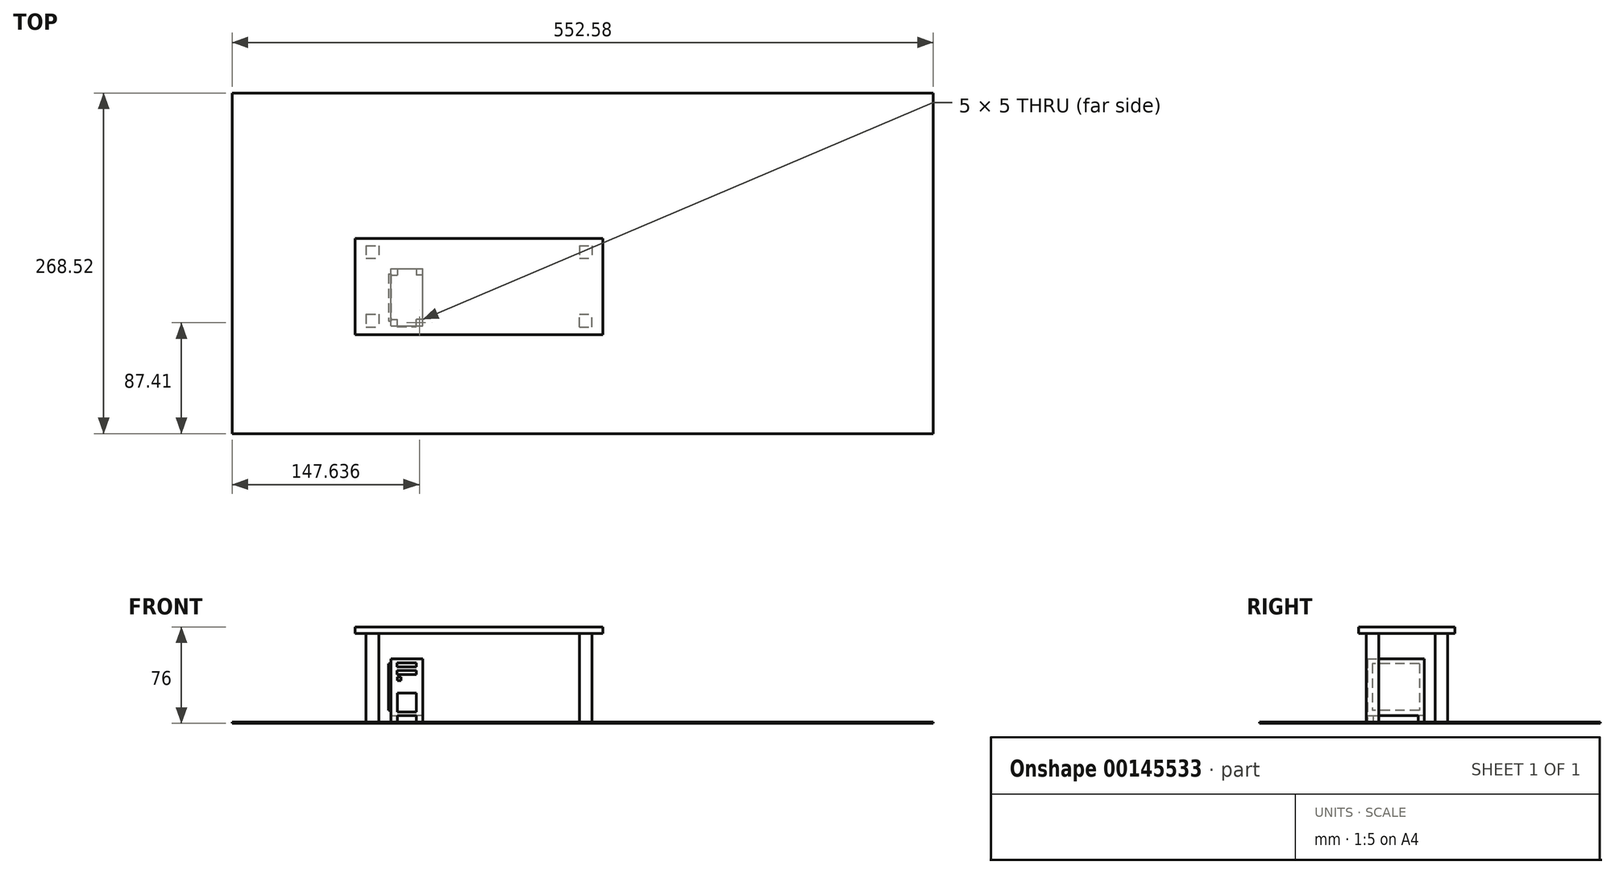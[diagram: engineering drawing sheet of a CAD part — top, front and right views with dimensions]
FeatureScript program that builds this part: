
annotation { "Feature Type Name" : "Feature", "Feature Type Description" : "" }
export const myFeature = defineFeature(function(context is Context, id is Id, definition is map)
    precondition{}
    {
        {
            var Q0;
            Q0=qCreatedBy(makeId("Front.planeOp"),FACE);
            var sketch = newSketch(context, id + "F0", { "sketchPlane" : qUnion([Q0])});
            skLineSegment(sketch, "E0.bottom", {"start": v(-65.78, 17.75) * mm, "end": v(-40.78, 17.75) * mm});
            skLineSegment(sketch, "E0.top", {"start": v(-65.78, -27.25) * mm, "end": v(-40.78, -27.25) * mm});
            skLineSegment(sketch, "E0.left", {"start": v(-65.78, 17.75) * mm, "end": v(-65.78, -27.25) * mm});
            skLineSegment(sketch, "E0.right", {"start": v(-40.78, 17.75) * mm, "end": v(-40.78, -27.25) * mm});
            skSolve(sketch);
        }
        {
            var Q0;
            Q0=makeQuery(id+"F0.imprint","IMPRINT",FACE,{"disambiguationData":[TD([[makeQuery(id+"F0.imprint","IMPRINT",EDGE,{"derivedFrom":sQuery(id+"F0.wireOp",EDGE,"E0.bottom")}),-1.0]])]});
            extrude(context, id + "F1", {"entities" : qUnion([Q0]), "depth" : 45 * mm});
        }
        {
            var Q0;
            Q0=makeQuery(id+"F1.opExtrude","SWEPT_FACE",FACE,{"disambiguationData":[OSD([sQuery(id+"F0.wireOp",EDGE,"E0.left")])]});
            var sketch = newSketch(context, id + "F2", { "sketchPlane" : qUnion([Q0])});
            skLineSegment(sketch, "E1.bottom", {"start": v(4.1, 13.7) * mm, "end": v(41.11, 13.7) * mm});
            skLineSegment(sketch, "E1.top", {"start": v(4.1, -23.11) * mm, "end": v(41.11, -23.11) * mm});
            skLineSegment(sketch, "E1.left", {"start": v(4.1, 13.7) * mm, "end": v(4.1, -23.11) * mm});
            skLineSegment(sketch, "E1.right", {"start": v(41.11, 13.7) * mm, "end": v(41.11, -23.11) * mm});
            skSolve(sketch);
        }
        {
            var Q0;
            Q0=makeQuery(id+"F2.imprint","IMPRINT",FACE,{"disambiguationData":[TD([[makeQuery(id+"F2.imprint","IMPRINT",EDGE,{"derivedFrom":sQuery(id+"F2.wireOp",EDGE,"E1.bottom")}),-1.0]])]});
            extrude(context, id + "F3", {"entities" : qUnion([Q0]), "depth" : 2 * mm});
        }
        {
            var Q0;
            Q0=makeQuery(id+"F1.opExtrude","CAP_FACE",FACE,{"disambiguationData":[OSD([sQuery(id+"F0.wireOp",EDGE,"E0.bottom"),sQuery(id+"F0.wireOp",EDGE,"E0.top"),sQuery(id+"F0.wireOp",EDGE,"E0.left"),sQuery(id+"F0.wireOp",EDGE,"E0.right")])],"isStart":false});
            var sketch = newSketch(context, id + "F4", { "sketchPlane" : qUnion([Q0])});
            skLineSegment(sketch, "E2.bottom", {"start": v(-60.89, 14.33) * mm, "end": v(-45.89, 14.33) * mm});
            skLineSegment(sketch, "E2.top", {"start": v(-60.89, 11.33) * mm, "end": v(-45.89, 11.33) * mm});
            skLineSegment(sketch, "E2.left", {"start": v(-60.89, 14.33) * mm, "end": v(-60.89, 11.33) * mm});
            skLineSegment(sketch, "E2.right", {"start": v(-45.89, 14.33) * mm, "end": v(-45.89, 11.33) * mm});
            skLineSegment(sketch, "E3.bottom", {"start": v(-60.89, 8.33) * mm, "end": v(-45.89, 8.33) * mm});
            skLineSegment(sketch, "E3.top", {"start": v(-60.89, 5.33) * mm, "end": v(-45.89, 5.33) * mm});
            skLineSegment(sketch, "E3.left", {"start": v(-60.89, 8.33) * mm, "end": v(-60.89, 5.33) * mm});
            skLineSegment(sketch, "E3.right", {"start": v(-45.89, 8.33) * mm, "end": v(-45.89, 5.33) * mm});
            skSolve(sketch);
        }
        {
            var Q0;
            Q0 = qSketchRegion(id + "F4", true);
            extrude(context, id + "F5", {"entities" : qUnion([Q0]), "depth" : 0.5 * mm});
        }
        {
            var Q0;
            Q0=makeQuery(id+"F1.opExtrude","CAP_FACE",FACE,{"disambiguationData":[OSD([sQuery(id+"F0.wireOp",EDGE,"E0.bottom"),sQuery(id+"F0.wireOp",EDGE,"E0.top"),sQuery(id+"F0.wireOp",EDGE,"E0.left"),sQuery(id+"F0.wireOp",EDGE,"E0.right")])],"isStart":false});
            var sketch = newSketch(context, id + "F6", { "sketchPlane" : qUnion([Q0])});
            skLineSegment(sketch, "E4.bottom", {"start": v(-60.78, -24.38) * mm, "end": v(-45.78, -24.38) * mm});
            skLineSegment(sketch, "E4.top", {"start": v(-60.78, -9.38) * mm, "end": v(-45.78, -9.38) * mm});
            skLineSegment(sketch, "E4.left", {"start": v(-60.78, -24.38) * mm, "end": v(-60.78, -9.38) * mm});
            skLineSegment(sketch, "E4.right", {"start": v(-45.78, -24.38) * mm, "end": v(-45.78, -9.38) * mm});
            skSolve(sketch);
        }
        {
            var Q0;
            Q0=makeQuery(id+"F6.imprint","IMPRINT",FACE,{"disambiguationData":[TD([[makeQuery(id+"F6.imprint","IMPRINT",EDGE,{"derivedFrom":sQuery(id+"F6.wireOp",EDGE,"E4.bottom")}),1.0]])]});
            extrude(context, id + "F7", {"entities" : qUnion([Q0]), "depth" : 0.5 * mm});
        }
        {
            var Q0;
            Q0=makeQuery(id+"F1.opExtrude","CAP_FACE",FACE,{"disambiguationData":[OSD([sQuery(id+"F0.wireOp",EDGE,"E0.bottom"),sQuery(id+"F0.wireOp",EDGE,"E0.top"),sQuery(id+"F0.wireOp",EDGE,"E0.left"),sQuery(id+"F0.wireOp",EDGE,"E0.right")])],"isStart":false});
            var sketch = newSketch(context, id + "F8", { "sketchPlane" : qUnion([Q0])});
            skLineSegment(sketch, "E5.bottom", {"start": v(-60.82, 3.4) * mm, "end": v(-57.82, 3.4) * mm});
            skLineSegment(sketch, "E5.top", {"start": v(-60.82, 0.4) * mm, "end": v(-57.82, 0.4) * mm});
            skLineSegment(sketch, "E5.left", {"start": v(-60.82, 3.4) * mm, "end": v(-60.82, 0.4) * mm});
            skLineSegment(sketch, "E5.right", {"start": v(-57.82, 3.4) * mm, "end": v(-57.82, 0.4) * mm});
            skSolve(sketch);
        }
        {
            var Q0;
            Q0=makeQuery(id+"F8.imprint","IMPRINT",FACE,{"disambiguationData":[TD([[makeQuery(id+"F8.imprint","IMPRINT",EDGE,{"derivedFrom":sQuery(id+"F8.wireOp",EDGE,"E5.bottom")}),-1.0]])]});
            extrude(context, id + "F9", {"entities" : qUnion([Q0]), "depth" : 0.5 * mm});
        }
        {
            var Q0;
            Q0=makeQuery(id+"F9.opExtrude","CAP_FACE",FACE,{"disambiguationData":[OSD([sQuery(id+"F8.wireOp",EDGE,"E5.bottom"),sQuery(id+"F8.wireOp",EDGE,"E5.top"),sQuery(id+"F8.wireOp",EDGE,"E5.left"),sQuery(id+"F8.wireOp",EDGE,"E5.right")])],"isStart":false});
            var sketch = newSketch(context, id + "F10", { "sketchPlane" : qUnion([Q0])});
            skSolve(sketch);
        }
        {
            var Q0;
            Q0=makeQuery(id+"F1.opExtrude","SWEPT_FACE",FACE,{"disambiguationData":[OSD([sQuery(id+"F0.wireOp",EDGE,"E0.top")])]});
            var sketch = newSketch(context, id + "F11", { "sketchPlane" : qUnion([Q0])});
            skLineSegment(sketch, "E6.bottom", {"start": v(-65.78, 45) * mm, "end": v(-60.78, 45) * mm});
            skLineSegment(sketch, "E6.top", {"start": v(-65.78, 40) * mm, "end": v(-60.78, 40) * mm});
            skLineSegment(sketch, "E6.left", {"start": v(-65.78, 45) * mm, "end": v(-65.78, 40) * mm});
            skLineSegment(sketch, "E6.right", {"start": v(-60.78, 45) * mm, "end": v(-60.78, 40) * mm});
            skLineSegment(sketch, "E7.bottom", {"start": v(-40.78, 45) * mm, "end": v(-45.78, 45) * mm});
            skLineSegment(sketch, "E7.top", {"start": v(-40.78, 40) * mm, "end": v(-45.78, 40) * mm});
            skLineSegment(sketch, "E7.left", {"start": v(-40.78, 45) * mm, "end": v(-40.78, 40) * mm});
            skLineSegment(sketch, "E7.right", {"start": v(-45.78, 45) * mm, "end": v(-45.78, 40) * mm});
            skLineSegment(sketch, "E8.bottom", {"start": v(-65.78, 0) * mm, "end": v(-60.78, 0) * mm});
            skLineSegment(sketch, "E8.top", {"start": v(-65.78, 5) * mm, "end": v(-60.78, 5) * mm});
            skLineSegment(sketch, "E8.left", {"start": v(-65.78, 0) * mm, "end": v(-65.78, 5) * mm});
            skLineSegment(sketch, "E8.right", {"start": v(-60.78, 0) * mm, "end": v(-60.78, 5) * mm});
            skLineSegment(sketch, "E9.bottom", {"start": v(-40.78, 0) * mm, "end": v(-45.78, 0) * mm});
            skLineSegment(sketch, "E9.top", {"start": v(-40.78, 5) * mm, "end": v(-45.78, 5) * mm});
            skLineSegment(sketch, "E9.left", {"start": v(-40.78, 0) * mm, "end": v(-40.78, 5) * mm});
            skLineSegment(sketch, "E9.right", {"start": v(-45.78, 0) * mm, "end": v(-45.78, 5) * mm});
            skSolve(sketch);
        }
        {
            var Q0;
            Q0 = qSketchRegion(id + "F11", true);
            extrude(context, id + "F12", {"entities" : qUnion([Q0]), "operationType" : NewBodyOperationType.ADD, "depth" : 5 * mm});
        }
        {
            var Q0;
            Q0=makeQuery(id+"F12.opExtrude","CAP_FACE",FACE,{"disambiguationData":[OSD([sQuery(id+"F11.wireOp",EDGE,"E7.bottom"),sQuery(id+"F11.wireOp",EDGE,"E7.top"),sQuery(id+"F11.wireOp",EDGE,"E7.left"),sQuery(id+"F11.wireOp",EDGE,"E7.right")])],"isStart":false});
            var sketch = newSketch(context, id + "F13", { "sketchPlane" : qUnion([Q0])});
            skLineSegment(sketch, "E10.bottom", {"start": v(-190.92, 129.9) * mm, "end": v(361.66, 129.9) * mm});
            skLineSegment(sketch, "E10.top", {"start": v(-190.92, -138.61) * mm, "end": v(361.66, -138.61) * mm});
            skLineSegment(sketch, "E10.left", {"start": v(-190.92, 129.9) * mm, "end": v(-190.92, -138.61) * mm});
            skLineSegment(sketch, "E10.right", {"start": v(361.66, 129.9) * mm, "end": v(361.66, -138.61) * mm});
            skSolve(sketch);
        }
        {
            var Q0;
            Q0=makeQuery(id+"F13.imprint","IMPRINT",FACE,{"disambiguationData":[TD([[makeQuery(id+"F13.imprint","IMPRINT",EDGE,{"derivedFrom":sQuery(id+"F13.wireOp",EDGE,"E10.bottom")}),-1.0]])]});
            extrude(context, id + "F14", {"entities" : qUnion([Q0]), "depth" : 1 * mm});
        }
        {
            var Q0;
            Q0=makeQuery(id+"F14.opExtrude","CAP_FACE",FACE,{"disambiguationData":[OSD([sQuery(id+"F11.wireOp",EDGE,"E7.bottom"),sQuery(id+"F11.wireOp",EDGE,"E7.top"),sQuery(id+"F11.wireOp",EDGE,"E7.left"),sQuery(id+"F11.wireOp",EDGE,"E7.right"),sQuery(id+"F13.wireOp",EDGE,"E10.bottom"),sQuery(id+"F13.wireOp",EDGE,"E10.top"),sQuery(id+"F13.wireOp",EDGE,"E10.left"),sQuery(id+"F13.wireOp",EDGE,"E10.right")])],"isStart":true});
            var sketch = newSketch(context, id + "F15", { "sketchPlane" : qUnion([Q0])});
            skLineSegment(sketch, "E11.bottom", {"start": v(-85.3, 18.36) * mm, "end": v(-75.3, 18.36) * mm});
            skLineSegment(sketch, "E11.top", {"start": v(-85.3, 8.36) * mm, "end": v(-75.3, 8.36) * mm});
            skLineSegment(sketch, "E11.left", {"start": v(-85.3, 18.36) * mm, "end": v(-85.3, 8.36) * mm});
            skLineSegment(sketch, "E11.right", {"start": v(-75.3, 18.36) * mm, "end": v(-75.3, 8.36) * mm});
            skLineSegment(sketch, "E12.bottom", {"start": v(82.79, 18.36) * mm, "end": v(92.79, 18.36) * mm});
            skLineSegment(sketch, "E12.top", {"start": v(82.79, 8.36) * mm, "end": v(92.79, 8.36) * mm});
            skLineSegment(sketch, "E12.left", {"start": v(82.79, 18.36) * mm, "end": v(82.79, 8.36) * mm});
            skLineSegment(sketch, "E12.right", {"start": v(92.79, 18.36) * mm, "end": v(92.79, 8.36) * mm});
            skLineSegment(sketch, "E13.bottom", {"start": v(-85.3, -35.9) * mm, "end": v(-75.3, -35.9) * mm});
            skLineSegment(sketch, "E13.top", {"start": v(-85.3, -45.9) * mm, "end": v(-75.3, -45.9) * mm});
            skLineSegment(sketch, "E13.left", {"start": v(-85.3, -35.9) * mm, "end": v(-85.3, -45.9) * mm});
            skLineSegment(sketch, "E13.right", {"start": v(-75.3, -35.9) * mm, "end": v(-75.3, -45.9) * mm});
            skLineSegment(sketch, "E14.bottom", {"start": v(82.79, -45.9) * mm, "end": v(92.79, -45.9) * mm});
            skLineSegment(sketch, "E14.top", {"start": v(82.79, -35.9) * mm, "end": v(92.79, -35.9) * mm});
            skLineSegment(sketch, "E14.left", {"start": v(82.79, -45.9) * mm, "end": v(82.79, -35.9) * mm});
            skLineSegment(sketch, "E14.right", {"start": v(92.79, -45.9) * mm, "end": v(92.79, -35.9) * mm});
            skSolve(sketch);
        }
        {
            var Q0;
            Q0 = qSketchRegion(id + "F15", true);
            extrude(context, id + "F16", {"entities" : qUnion([Q0]), "depth" : 70 * mm});
        }
        {
            var Q0;
            Q0=makeQuery(id+"F16.opExtrude","CAP_FACE",FACE,{"disambiguationData":[OSD([sQuery(id+"F15.wireOp",EDGE,"E14.bottom"),sQuery(id+"F15.wireOp",EDGE,"E14.top"),sQuery(id+"F15.wireOp",EDGE,"E14.left"),sQuery(id+"F15.wireOp",EDGE,"E14.right")])],"isStart":false});
            var sketch = newSketch(context, id + "F17", { "sketchPlane" : qUnion([Q0])});
            skLineSegment(sketch, "E15.bottom", {"start": v(-93.93, 23.97) * mm, "end": v(101.18, 23.97) * mm});
            skLineSegment(sketch, "E15.top", {"start": v(-93.93, -51.97) * mm, "end": v(101.18, -51.97) * mm});
            skLineSegment(sketch, "E15.left", {"start": v(-93.93, 23.97) * mm, "end": v(-93.93, -51.97) * mm});
            skLineSegment(sketch, "E15.right", {"start": v(101.18, 23.97) * mm, "end": v(101.18, -51.97) * mm});
            skSolve(sketch);
        }
        {
            var Q0;
            Q0 = qSketchRegion(id + "F17", true);
            extrude(context, id + "F18", {"entities" : qUnion([Q0]), "depth" : 5 * mm});
        }
    });
